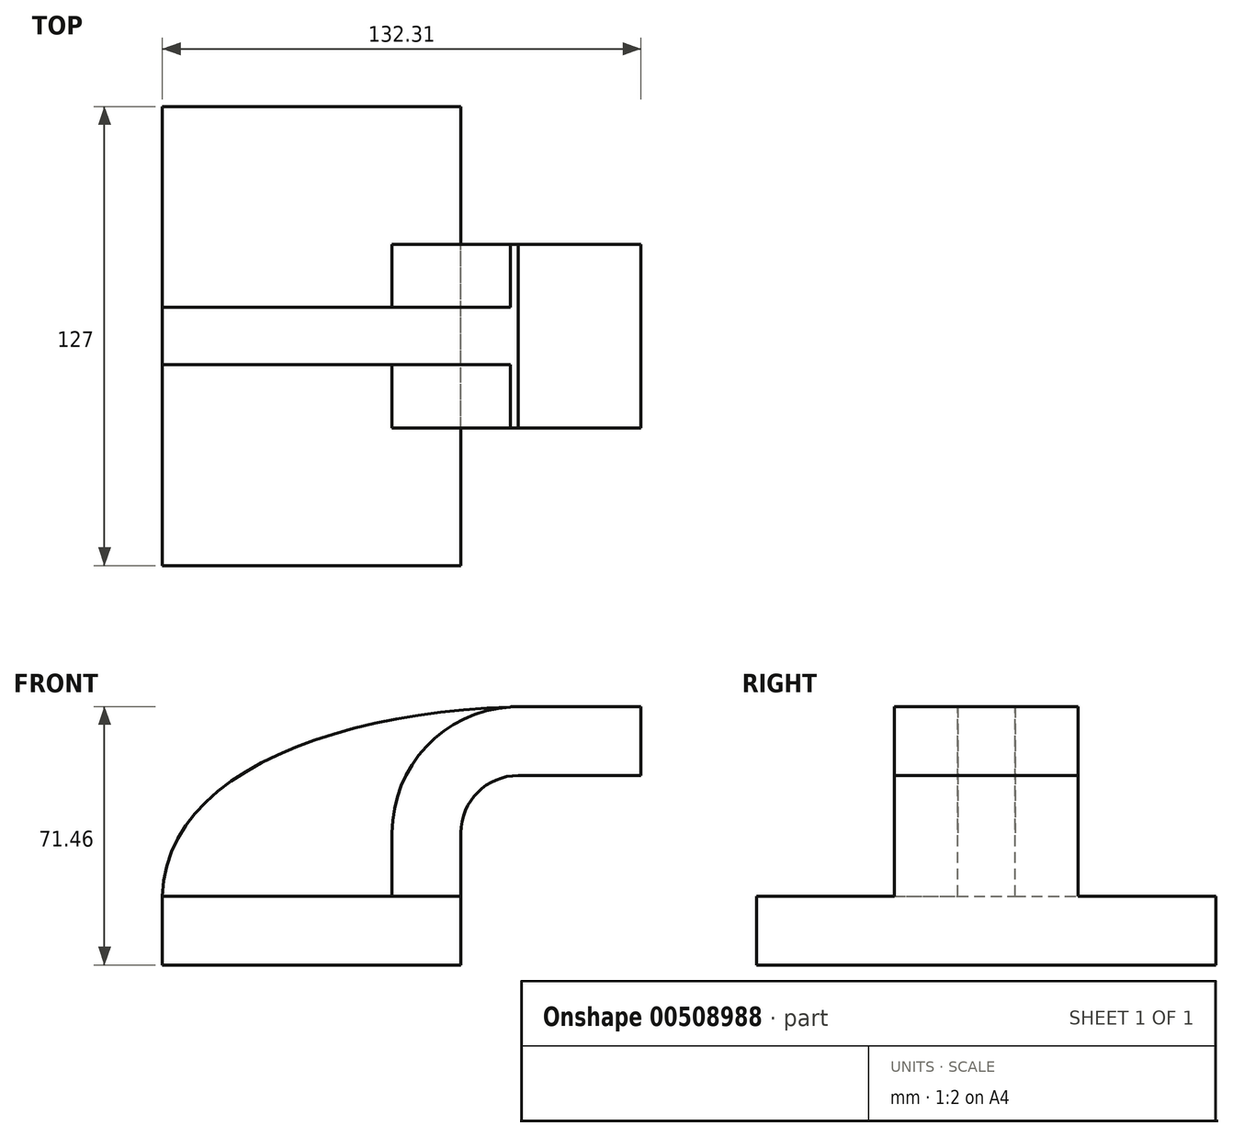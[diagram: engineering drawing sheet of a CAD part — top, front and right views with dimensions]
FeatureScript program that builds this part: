
annotation { "Feature Type Name" : "Feature", "Feature Type Description" : "" }
export const myFeature = defineFeature(function(context is Context, id is Id, definition is map)
    precondition{}
    {
        {
            var Q0;
            Q0=qCreatedBy(makeId("Front.planeOp"),FACE);
            var sketch = newSketch(context, id + "F0", { "sketchPlane" : qUnion([Q0])});
            skLineSegment(sketch, "E0.bottom", {"start": v(-41.28, 9.52) * mm, "end": v(41.27, 9.53) * mm});
            skLineSegment(sketch, "E0.top", {"start": v(-41.28, -9.53) * mm, "end": v(41.28, -9.53) * mm});
            skLineSegment(sketch, "E0.left", {"start": v(-41.28, 9.52) * mm, "end": v(-41.27, -9.53) * mm});
            skLineSegment(sketch, "E0.right", {"start": v(41.28, 9.53) * mm, "end": v(41.28, -9.52) * mm});
            skPoint(sketch, "E0.middle", {"position": v(0, 0) * mm});
            skLineSegment(sketch, "E1.bottom", {"start": v(60.32, 38.1) * mm, "end": v(111.12, 38.1) * mm});
            skLineSegment(sketch, "E1.top", {"start": v(60.32, 66.68) * mm, "end": v(111.12, 66.68) * mm});
            skLineSegment(sketch, "E1.left", {"start": v(60.32, 38.1) * mm, "end": v(60.32, 66.68) * mm});
            skLineSegment(sketch, "E1.right", {"start": v(111.12, 38.1) * mm, "end": v(111.12, 66.68) * mm});
            skPoint(sketch, "E1.middle", {"position": v(85.72, 52.39) * mm});
            skLineSegment(sketch, "E2", {"start": v(41.27, 9.53) * mm, "end": v(41.27, 27) * mm});
            skArc(sketch, "E3", {"start": v(41.27, 27) * mm, "mid": v(45.92, 38.23) * mm, "end": v(57.15, 42.88) * mm});
            skLineSegment(sketch, "E4", {"start": v(57.15, 42.88) * mm, "end": v(91.03, 42.88) * mm});
            skLineSegment(sketch, "E5.0", {"start": v(57.15, 61.93) * mm, "end": v(91.03, 61.93) * mm});
            skArc(sketch, "E5.1", {"start": v(22.22, 27) * mm, "mid": v(32.45, 51.7) * mm, "end": v(57.15, 61.93) * mm});
            skLineSegment(sketch, "E5.2", {"start": v(22.23, 9.53) * mm, "end": v(22.23, 27) * mm});
            skLineSegment(sketch, "E6", {"start": v(91.03, 38.1) * mm, "end": v(91.03, 66.68) * mm});
            skPoint(sketch, "E6.startSnap0", {"position": v(85.72, 38.1) * mm});
            skFitSpline(sketch, "E7", {"points": [v(-41.28, 9.53) * mm, v(57.15, 61.93) * mm], "startDerivative": vector(2.17, 101.65) * mm, "endDerivative": vector(152.6, 4.15) * mm});
            skSolve(sketch);
        }
        {
            var Q0;
            Q0=makeQuery(id+"F0.imprint","IMPRINT",FACE,{"disambiguationData":[TD([[makeQuery(id+"F0.imprint","IMPRINT",EDGE,{"derivedFrom":sQuery(id+"F0.wireOp",EDGE,"E0.top")}),1.0]])]});
            extrude(context, id + "F1", {"entities" : qUnion([Q0]), "endBound" : BoundingType.SYMMETRIC, "depth" : 127 * mm});
        }
        {
            var Q0;
            {var subQ1=sQuery(id+"F0.wireOp",EDGE,"E2");Q0=makeQuery(id+"F0.imprint","IMPRINT",FACE,{"disambiguationData":[TD([[makeQuery(id+"F0.imprint","IMPRINT",EDGE,{"derivedFrom":subQ1}),1.0]])]});}
            var Q1;
            {var subQ0=sQuery(id+"F0.wireOp",EDGE,"E4");var subQ1=sQuery(id+"F0.wireOp",EDGE,"E1.left");var subQ2=makeQuery(id+"F0.imprint","INTERSECT",VERTEX,{"derivedFrom":[subQ1,subQ0]});Q1=makeQuery(id+"F0.imprint","IMPRINT",FACE,{"disambiguationData":[TD([[makeQuery(id+"F0.imprint","IMPRINT",EDGE,{"disambiguationData":[TD([[subQ2,-1.0]])],"derivedFrom":subQ1}),-1.0]])]});}
            extrude(context, id + "F2", {"entities" : qUnion([Q0, Q1]), "operationType" : NewBodyOperationType.ADD, "endBound" : BoundingType.SYMMETRIC, "depth" : 50.8 * mm});
        }
        {
            var Q0;
            {var subQ3=sQuery(id+"F0.wireOp",EDGE,"E5.2");Q0=makeQuery(id+"F0.imprint","IMPRINT",FACE,{"disambiguationData":[TD([[makeQuery(id+"F0.imprint","IMPRINT",EDGE,{"derivedFrom":subQ3}),1.0]])]});}
            extrude(context, id + "F3", {"entities" : qUnion([Q0]), "operationType" : NewBodyOperationType.ADD, "endBound" : BoundingType.SYMMETRIC, "depth" : 15.88 * mm});
        }
    });
